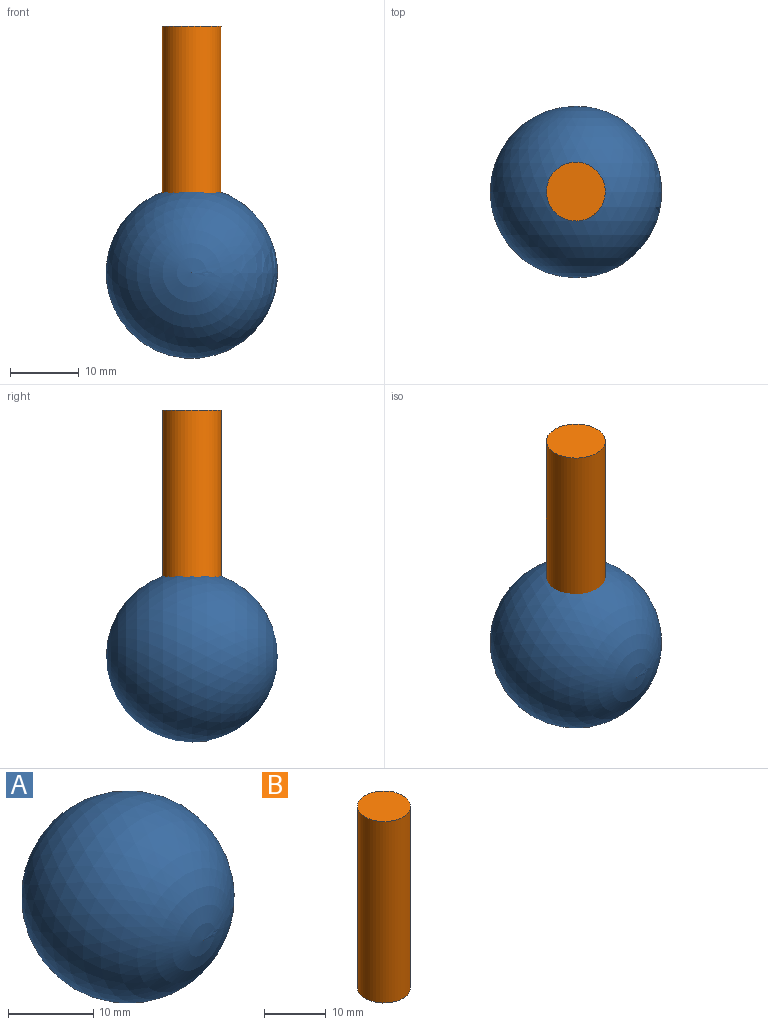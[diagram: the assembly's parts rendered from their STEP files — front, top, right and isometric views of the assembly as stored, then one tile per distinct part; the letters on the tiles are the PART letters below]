
ASSEMBLY  parts=2 mates=1
PART A: 1 faces, bbox 25x25x25 mm
  f0: sphere r=12.5mm, area 1963.5mm2
PART B: 3 faces, bbox 8.6x8.6x36 mm
  f0: cylinder r=4.29mm len=35.95mm, axis (0,0,-1), area 969.9mm2, adj f1,f2
  f1: plane 8.59x8.59mm, normal (0,0,-1), area 57.9mm2, adj f0
  f2: plane 8.59x8.59mm, normal (0,0,1), area 57.9mm2, adj f0
PLACE A t=(-50.02,0,0)mm
PLACE B t=(13.64,1.57,0)mm
MATE fastened B.f0 <-> A.f0  axis (0,0,-1) through (-18.17,1.57,0)mm
